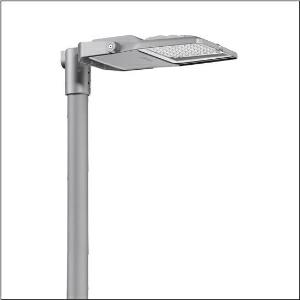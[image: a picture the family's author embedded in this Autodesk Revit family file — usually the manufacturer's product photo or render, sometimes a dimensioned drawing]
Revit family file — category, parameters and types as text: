
# Revit family: floodlight_fl_21_iq_mini___pl61_5xa7771d4c3a_f55b
name_source: partatom
category: Lighting Fixtures
units: mm (PartAtom-declared; Revit-internal decimal feet)

## family parameters
Cut with Voids When Loaded = No
Host = Face
Light Source = No
Part Type = Normal
Room Calculation Point = No
Round Connector Dimension = Use Diameter
Shared = No

## types (1)
- --- (1 x LED, 18260 lm, 143 W, 4000K)
    Apparent Load = 143 VA
    CIE Flux Codes = 33 65 98 100 100
    Color Rendering = 70
    Color Temperature = 4000K
    Default Elevation = 1800 mm
    Description = Floodlight FL 21 iQ mini, floodlight, primary light control with lens, of PMMA, primary optical cover: protective disc, of toughened safety glass, transparent, light distribution: PL61, light emission: direct distribution, installation type: surface-mounted, LED, High Power LED, rated luminous flux: 18.260lm, luminous efficacy: 128lm/W, light colour: 740, colour temperature: 4000K, control: Auto-Match, Temp-Guard, Lumen-Switch, Night-Set, Smart-Wire, Light-Fading, Desk-Remote (wireless, voltage-free reading and setting of iQ features in the workshop via application-optimized NFC function/RFID function), optimised constant luminous flux control (CLO 2.0), with terminal, 6-pole, mains connection: 220..240V, AC, 50/60Hz, start of lifetime: 143W, end of service life: 152W, reduction: 61W, luminaire housing, of diecast aluminium, powder-coated, Siteco® metallic grey (DB 702S), corrosivity category C5 mid according to DIN EN ISO 12944, sealing non-destructively replaceable, please order mast flange separately, mast bracket, of steel, galvanised, powder-coated, Siteco® metallic grey (DB 702S), protection rating (complete): IP66, insulation class (complete): insulation class II (safety insulation), certification: CE, ENEC, VDE, protection symbol: D, impact resistance: IK08, permissible operating ambient temperature: -40..+40°C, permissible operating ambient temperature for outdoor applications: -40..+50°C, standard: DIN EN 12944, LABS conformity tested according to VDMA 24364:2018-05, packaging unit: 1 piece

Light Distribution: PL61
    Height = 70 mm
    Lamp = 1 x LED
    Lamp Light Flux = 18260 lm
    Lamp Power = 143 W
    Lamp count = 1
    Length = 485 mm
    Luminous efficacy = 128 lm/W
    Manufacturer = Siteco
    ModVariant = No
    Model = 5XA7771D4C3A
    Number of Poles = 1
    OnlyDefault = Yes
    Power Factor = 1
    Product Name = Floodlight FL 21 iQ mini | PL61
    Product group = floodlight | pylon annexe
    ProductGroupID = 6200
    Protection Class = Protection class II
    Protection Degree = IP 66
    RLX_Detail_Level = 1
    RLX_Emergency_Light_Flux = 0 lm
    RLX_Emergency_Type = 0
    RLX_Emergency_Type_DB = No
    RlxData = <blob elided: 101677 chars, md5=9a3101f4>
    Socket = socket
    Standby Power = 0 W
    System Light Flux = 18260 lm
    System Power = 143 W
    Type Comments = factory setting: luminous flux: 100 % | dim-lin: 254 | 730 mA
    Type Image = l_1007125.jpg
    URL = http://relux.com
    VarID = @adj_143713
    Voltage = 0 V
    Weight = 0.00 kg
    Width = 337 mm

## geometry (parser evidence)
native form markers: Blend x4, Sweep x11
no freeform markers — native parametric forms only
